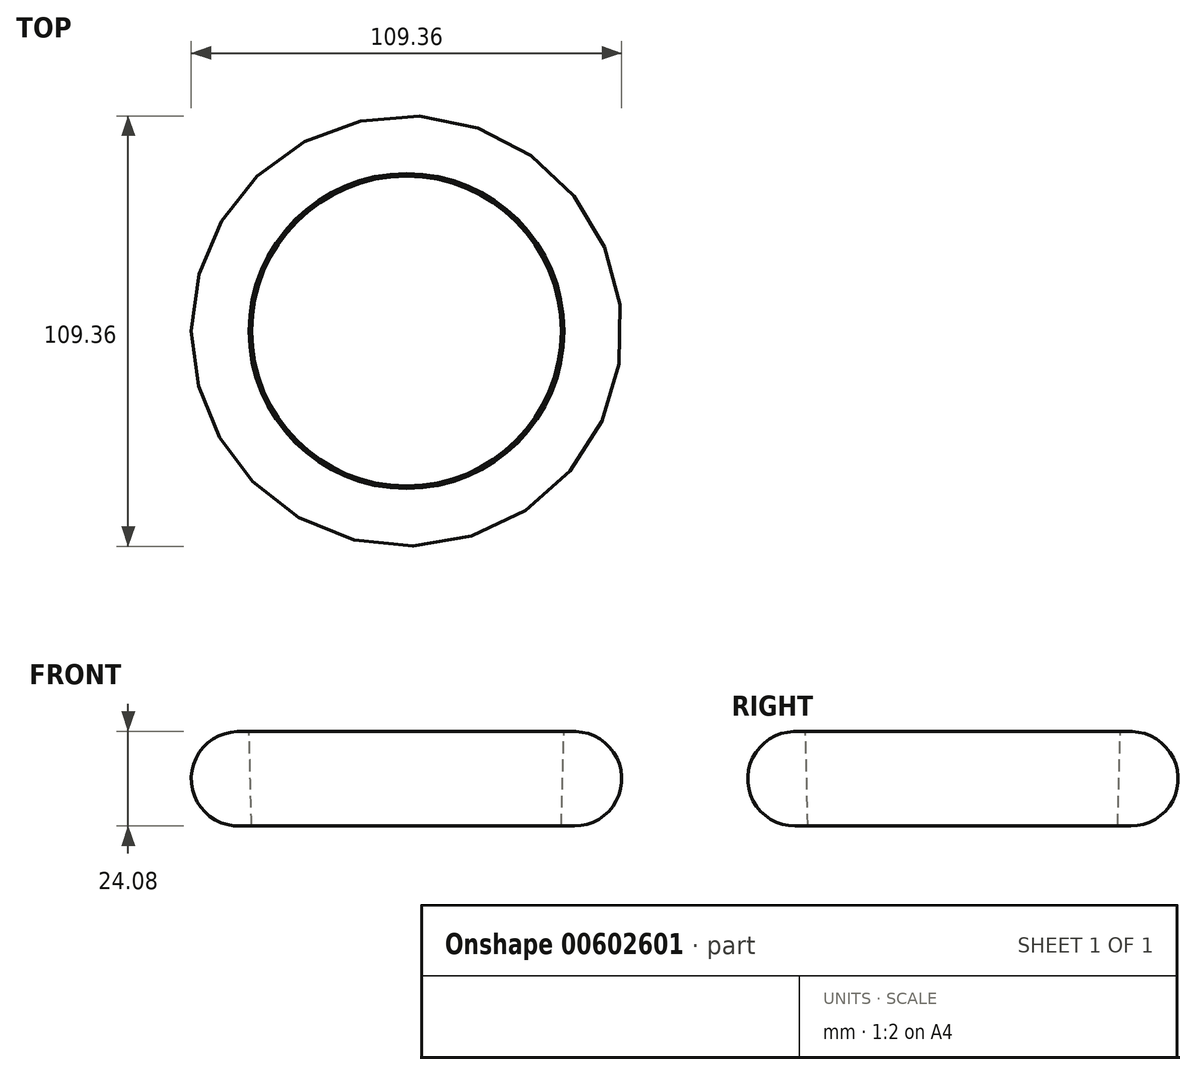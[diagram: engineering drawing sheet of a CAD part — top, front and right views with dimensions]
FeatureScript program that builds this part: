
annotation { "Feature Type Name" : "Feature", "Feature Type Description" : "" }
export const myFeature = defineFeature(function(context is Context, id is Id, definition is map)
    precondition{}
    {
        {
            var Q0;
            Q0=qCreatedBy(makeId("Top.planeOp"),FACE);
            var sketch = newSketch(context, id + "F0", { "sketchPlane" : qUnion([Q0])});
            skCircle(sketch, "E0", {"center": v(0, 0) * mm, "radius": 40 * mm});
            skSolve(sketch);
        }
        {
            var Q0;
            Q0=qCreatedBy(makeId("Front.planeOp"),FACE);
            var sketch = newSketch(context, id + "F1", { "sketchPlane" : qUnion([Q0])});
            skArc(sketch, "E1", {"start": v(-43, 12) * mm, "mid": v(-54.68, -0.32) * mm, "end": v(-42.35, -12) * mm});
            skLineSegment(sketch, "E2", {"start": v(-43, 12) * mm, "end": v(-40, 12.08) * mm});
            skLineSegment(sketch, "E3", {"start": v(-42.35, -12) * mm, "end": v(-39.35, -11.92) * mm});
            skLineSegment(sketch, "E4", {"start": v(-40, 12.08) * mm, "end": v(-39.35, -11.92) * mm});
            skSolve(sketch);
        }
        {
            var Q0;
            Q0 = qSketchRegion(id + "F1", true);
            var Q1;
            Q1 = qConstructionFilter(qBodyType(qCreatedBy(id + "F0" ,EDGE), BodyType.WIRE), ConstructionObject.NO);
            sweep(context, id + "F2", {"profiles" : qUnion([Q0]), "path" : qUnion([Q1])});
        }
        {
            var Q0;
            Q0=qCreatedBy(makeId("Right.planeOp"),FACE);
            cPlane(context, id + "F3", {"entities" : qUnion([Q0]), "cplaneType" : CPlaneType.OFFSET, "offset" : 40 * mm, "width" : 150 * mm, "height" : 150 * mm});
        }
    });
